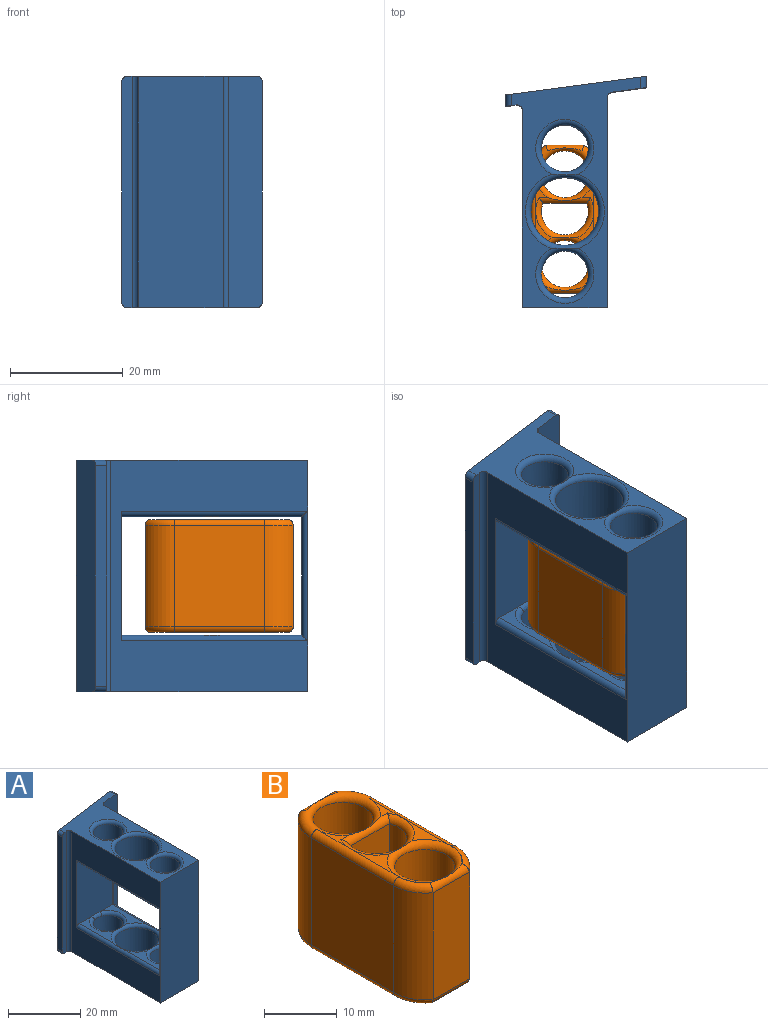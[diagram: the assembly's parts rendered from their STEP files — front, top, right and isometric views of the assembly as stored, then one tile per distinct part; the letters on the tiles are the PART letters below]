
ASSEMBLY  parts=2 mates=1
PART A: 55 faces, bbox 25x41.5x41.1 mm
  f0: plane 13.4x4.77mm, normal (0,0,1), area 26.7mm2, adj f22,f36,f39,f41
  f1: plane 13.4x4.77mm, normal (0,0,1), area 26.7mm2, adj f23,f34,f39,f41
  f2: plane 13.4x4.77mm, normal (0,0,1), area 26.7mm2, adj f22,f35,f36,f39
  f3: plane 13.4x4.77mm, normal (0,0,-1), area 26.7mm2, adj f23,f33,f37,f40
  f4: plane 13.4x4.77mm, normal (0,0,-1), area 26.7mm2, adj f22,f31,f37,f40
  f5: plane 13.4x4.77mm, normal (0,0,-1), area 26.7mm2, adj f23,f32,f33,f37
  f6: plane 41x37.12mm, normal (1,0,0), area 740.1mm2, adj f11,f18,f19,f40,f41,f42,f53
  f7: plane 41x34.86mm, normal (-1,0,0), area 670.2mm2, adj f11,f18,f19,f22,f32,f35,f54
  f8: cylinder r=4.15mm len=8.3mm, axis (0,0,-1), area 208.6mm2, adj f28,f31,f46
  f9: cylinder r=4.15mm len=8.3mm, axis (0,0,1), area 208.6mm2, adj f26,f33,f48
  f10: cylinder r=6mm len=12mm, axis (0,0,1), area 301.6mm2, adj f37,f47
  f11: plane 40.79x22.91mm, normal (0,0,-1), area 287.1mm2, adj f6,f7,f12,f13,f16,f19,f43,f44
  f12: plane 41.06x24.97mm, normal (-0.13,0.99,0), area 1029.6mm2, adj f11,f14,f15,f18,f49,f50,f51,f52
  f13: plane 41.06x6.13mm, normal (0.13,-0.99,0), area 250.7mm2, adj f11,f14,f18,f50,f52,f53
  f14: plane 39x2mm, normal (1,0,0), area 78mm2, adj f12,f13,f50,f52
  f15: plane 39x2mm, normal (-1,0,0), area 78mm2, adj f12,f16,f49,f51
  f16: plane 41.06x1.9mm, normal (0.13,-0.99,0), area 75.7mm2, adj f11,f15,f18,f49,f51,f54
  f17: cylinder r=4.15mm len=8.3mm, axis (0,0,-1), area 208.6mm2, adj f30,f36,f43
  f18: plane 40.79x22.91mm, normal (0,0,1), area 287.1mm2, adj f6,f7,f12,f13,f16,f19,f46,f47
  f19: plane 41x15mm, normal (0,-1,0), area 615mm2, adj f6,f7,f11,f18,f29,f38
  f20: cylinder r=4.15mm len=8.3mm, axis (0,0,1), area 208.6mm2, adj f27,f34,f44
  f21: cylinder r=6mm len=12mm, axis (0,0,1), area 301.6mm2, adj f39,f45
  f22: plane 23.03x14.03mm, normal (0,-1,0), area 294.4mm2, adj f0,f2,f4,f7,f24,f28,f30,f32
  f23: plane 21.03x13.03mm, normal (0,1,0), area 273mm2, adj f1,f3,f5,f25,f26,f27,f29,f38
  f24: plane 13.4x4.77mm, normal (0,0,-1), area 26.7mm2, adj f22,f31,f32,f37
  f25: plane 13.4x4.77mm, normal (0,0,1), area 26.7mm2, adj f23,f34,f35,f39
  f26: bspline ~4.08x1.11mm, area 4.2mm2, adj f9,f23,f33
  f27: bspline ~4.08x1.11mm, area 4.2mm2, adj f20,f23,f34
  f28: bspline ~4.08x1.11mm, area 4.2mm2, adj f8,f22,f31
  f29: cylinder r=1mm len=23mm, axis (0,0,-1), area 34.6mm2, adj f19,f23,f32,f35
  f30: bspline ~4.08x1.11mm, area 4.2mm2, adj f17,f22,f36
  f31: torus R=5.15mm, axis (0,0,-1), area 38.4mm2, adj f4,f8,f24,f28,f37
  f32: cylinder r=1mm len=33mm, axis (0,-1,0), area 50.2mm2, adj f5,f7,f22,f24,f29,f37
  f33: torus R=5.15mm, axis (0,0,-1), area 38mm2, adj f3,f5,f9,f26,f37
  f34: torus R=5.15mm, axis (0,0,-1), area 38mm2, adj f1,f20,f25,f27,f39
  f35: cylinder r=1mm len=33mm, axis (0,1,0), area 50.2mm2, adj f2,f7,f22,f25,f29,f39
  f36: torus R=5.15mm, axis (0,0,-1), area 38.4mm2, adj f0,f2,f17,f30,f39
  f37: torus R=7mm, axis (0,0,-1), area 58.2mm2, adj f3,f4,f5,f10,f24,f31,f32,f33
  f38: cylinder r=1mm len=23mm, axis (0,0,1), area 34.6mm2, adj f19,f23,f40,f41
  f39: torus R=7mm, axis (0,0,-1), area 58.2mm2, adj f0,f1,f2,f21,f25,f34,f35,f36
  f40: cylinder r=1mm len=34mm, axis (0,1,0), area 51mm2, adj f3,f4,f6,f37,f38,f42
  f41: cylinder r=1mm len=34mm, axis (0,-1,0), area 51mm2, adj f0,f1,f6,f38,f39,f42
  f42: cylinder r=1mm len=23mm, axis (0,0,-1), area 34.6mm2, adj f6,f22,f40,f41
  f43: torus R=5.15mm, axis (0,0,-1), area 42.9mm2, adj f11,f17,f45
  f44: torus R=5.15mm, axis (0,0,-1), area 42.9mm2, adj f11,f20,f45
  f45: torus R=7mm, axis (0,0,-1), area 59.5mm2, adj f11,f21,f43,f44
  f46: torus R=5.15mm, axis (0,0,-1), area 42.9mm2, adj f8,f18,f47
  f47: torus R=7mm, axis (0,0,-1), area 59.5mm2, adj f10,f18,f46,f48
  f48: torus R=5.15mm, axis (0,0,-1), area 42.9mm2, adj f9,f18,f47
  f49: cylinder r=1mm len=2.13mm, axis (0,1,0), area 3.1mm2, adj f12,f15,f16,f18
  f50: cylinder r=1mm len=2.13mm, axis (0,-1,0), area 3.1mm2, adj f12,f13,f14,f18
  f51: cylinder r=1mm len=2.13mm, axis (0,-1,0), area 3.1mm2, adj f11,f12,f15,f16
  f52: cylinder r=1mm len=2.13mm, axis (0,1,0), area 3.1mm2, adj f11,f12,f13,f14
  f53: cylinder r=1mm len=41mm, axis (0,0,-1), area 59mm2, adj f6,f11,f13,f18
  f54: cylinder r=1mm len=41mm, axis (0,0,-1), area 69.8mm2, adj f7,f11,f16,f18
PART B: 44 faces, bbox 13.3x28.9x20 mm
  f0: plane 4.15x2.1mm, normal (0,0,1), area 0.2mm2, adj f36,f39,f40,f41
  f1: plane 9.3x2.94mm, normal (0,0,1), area 7.7mm2, adj f36,f37,f40
  f2: plane 6.6x2.1mm, normal (0,0,1), area 3.1mm2, adj f34,f35,f36,f37
  f3: plane 9.3x2.94mm, normal (0,0,1), area 7.7mm2, adj f37,f40,f42
  f4: plane 4.15x2.1mm, normal (0,0,1), area 0.2mm2, adj f40,f41,f42,f43
  f5: plane 4.15x2.1mm, normal (0,0,-1), area 0.2mm2, adj f27,f29,f30,f31
  f6: plane 9.3x2.94mm, normal (0,0,-1), area 7.7mm2, adj f26,f27,f29
  f7: plane 6.6x2.1mm, normal (0,0,-1), area 3.1mm2, adj f24,f25,f26,f27
  f8: plane 4.15x2.1mm, normal (0,0,-1), area 0.2mm2, adj f29,f31,f32,f33
  f9: plane 9.3x2.94mm, normal (0,0,-1), area 7.7mm2, adj f26,f29,f32
  f10: cylinder r=6.15mm len=18mm, axis (0,0,-1), area 109.9mm2, adj f11,f21,f24,f35
  f11: plane 18x6.72mm, normal (0,1,0), area 121mm2, adj f10,f12,f28,f38
  f12: cylinder r=6.15mm len=18mm, axis (0,0,-1), area 109.9mm2, adj f11,f13,f24,f35
  f13: plane 18x16mm, normal (-1,0,0), area 288mm2, adj f12,f14,f27,f36
  f14: cylinder r=6.15mm len=18mm, axis (0,0,-1), area 106.6mm2, adj f13,f15,f30,f39
  f15: plane 18x7.02mm, normal (0,-1,0), area 126.4mm2, adj f14,f16,f31,f41
  f16: cylinder r=6.15mm len=18mm, axis (0,0,-1), area 106.6mm2, adj f15,f21,f33,f43
  f17: cylinder r=4.15mm len=18mm, axis (0,0,-1), area 288mm2, adj f20,f26,f37
  f18: cylinder r=4.15mm len=18mm, axis (0,0,-1), area 469.4mm2, adj f24,f35
  f19: cylinder r=4.15mm len=18mm, axis (0,0,-1), area 469.4mm2, adj f29,f40
  f20: plane 18x7.78mm, normal (0,-1,0), area 140mm2, adj f17,f25,f34
  f21: plane 18x16mm, normal (1,0,0), area 288mm2, adj f10,f16,f32,f42
  f22: plane 6.6x2.1mm, normal (0,0,1), area 3.1mm2, adj f34,f35,f37,f42
  f23: plane 6.6x2.1mm, normal (0,0,-1), area 3.1mm2, adj f24,f25,f26,f32
  f24: torus R=5.15mm, axis (0,0,1), area 57.7mm2, adj f7,f10,f12,f18,f23,f25,f27,f28
  f25: cylinder r=1mm len=9.06mm, axis (1,0,0), area 11.1mm2, adj f7,f20,f23,f24,f26
  f26: torus R=5.15mm, axis (0,0,1), area 26.8mm2, adj f6,f7,f9,f17,f23,f25,f29
  f27: cylinder r=1mm len=16mm, axis (0,-1,0), area 25.1mm2, adj f5,f6,f7,f13,f24,f30
  f28: cylinder r=1mm len=6.72mm, axis (-1,0,0), area 8mm2, adj f11,f24
  f29: torus R=5.15mm, axis (0,0,1), area 40.8mm2, adj f5,f6,f8,f9,f19,f26,f31
  f30: torus R=5.15mm, axis (0,0,1), area 8.5mm2, adj f5,f14,f27,f31
  f31: cylinder r=1mm len=7.02mm, axis (1,0,0), area 8.6mm2, adj f5,f8,f15,f29,f30,f33
  f32: cylinder r=1mm len=16mm, axis (0,1,0), area 25.1mm2, adj f8,f9,f21,f23,f24,f33
  f33: torus R=5.15mm, axis (0,0,1), area 8.5mm2, adj f8,f16,f31,f32
  f34: cylinder r=1mm len=9.06mm, axis (-1,0,0), area 11.1mm2, adj f2,f20,f22,f35,f37
  f35: torus R=5.15mm, axis (0,0,1), area 57.7mm2, adj f2,f10,f12,f18,f22,f34,f36,f38
  f36: cylinder r=1mm len=16mm, axis (0,1,0), area 25.1mm2, adj f0,f1,f2,f13,f35,f39
  f37: torus R=5.15mm, axis (0,0,1), area 26.8mm2, adj f1,f2,f3,f17,f22,f34,f40
  f38: cylinder r=1mm len=6.72mm, axis (1,0,0), area 8mm2, adj f11,f35
  f39: torus R=5.15mm, axis (0,0,1), area 8.5mm2, adj f0,f14,f36,f41
  f40: torus R=5.15mm, axis (0,0,1), area 40.8mm2, adj f0,f1,f3,f4,f19,f37,f41
  f41: cylinder r=1mm len=7.02mm, axis (-1,0,0), area 8.6mm2, adj f0,f4,f15,f39,f40,f43
  f42: cylinder r=1mm len=16mm, axis (0,-1,0), area 25.1mm2, adj f3,f4,f21,f22,f35,f43
  f43: torus R=5.15mm, axis (0,0,1), area 8.5mm2, adj f4,f16,f41,f42
PLACE A t=(-20.17,11.71,-9.24)mm
PLACE B t=(-20.17,-8.04,-7.74)mm
MATE revolute B.f17 <-> A.f37  axis (0,0,1) through (-20.17,-11.29,12.26)mm
